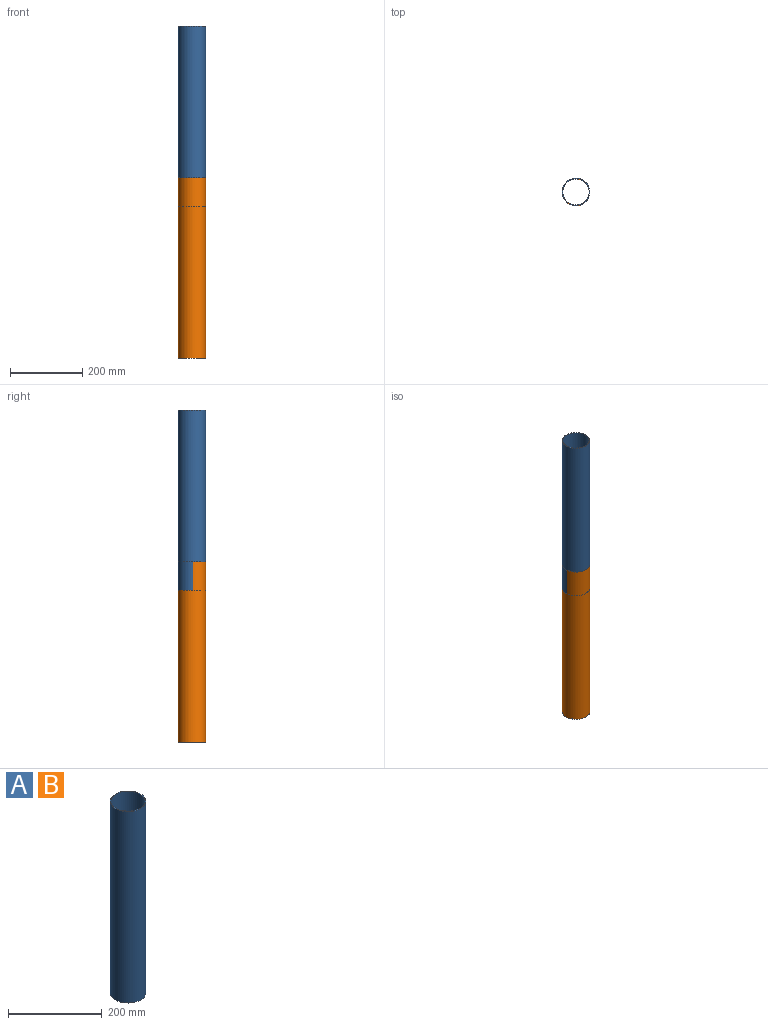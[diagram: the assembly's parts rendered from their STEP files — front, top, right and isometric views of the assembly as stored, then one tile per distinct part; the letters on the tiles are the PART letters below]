
ASSEMBLY  parts=2 mates=1
PART A: 4 faces, bbox 76x76x500 mm
  f0: cylinder r=36.5mm len=500mm, axis (0,0,-1), area 114668.1mm2, adj f2,f3
  f1: cylinder r=38mm len=500mm, axis (0,0,-1), area 119380.5mm2, adj f2,f3
  f2: plane 76x76mm, normal (0,0,1), area 351.1mm2, adj f0,f1
  f3: plane 76x76mm, normal (0,0,-1), area 351.1mm2, adj f0,f1
PART B: same geometry as A
PLACE A rot(axis=(1,0,0),180deg) t=(432.29,287.98,1550.58)mm
PLACE B t=(432.29,297.51,630.58)mm
MATE fastened B.f0 <-> A.f0  axis (0,0,1) through (432.29,292.75,1130.58)mm
